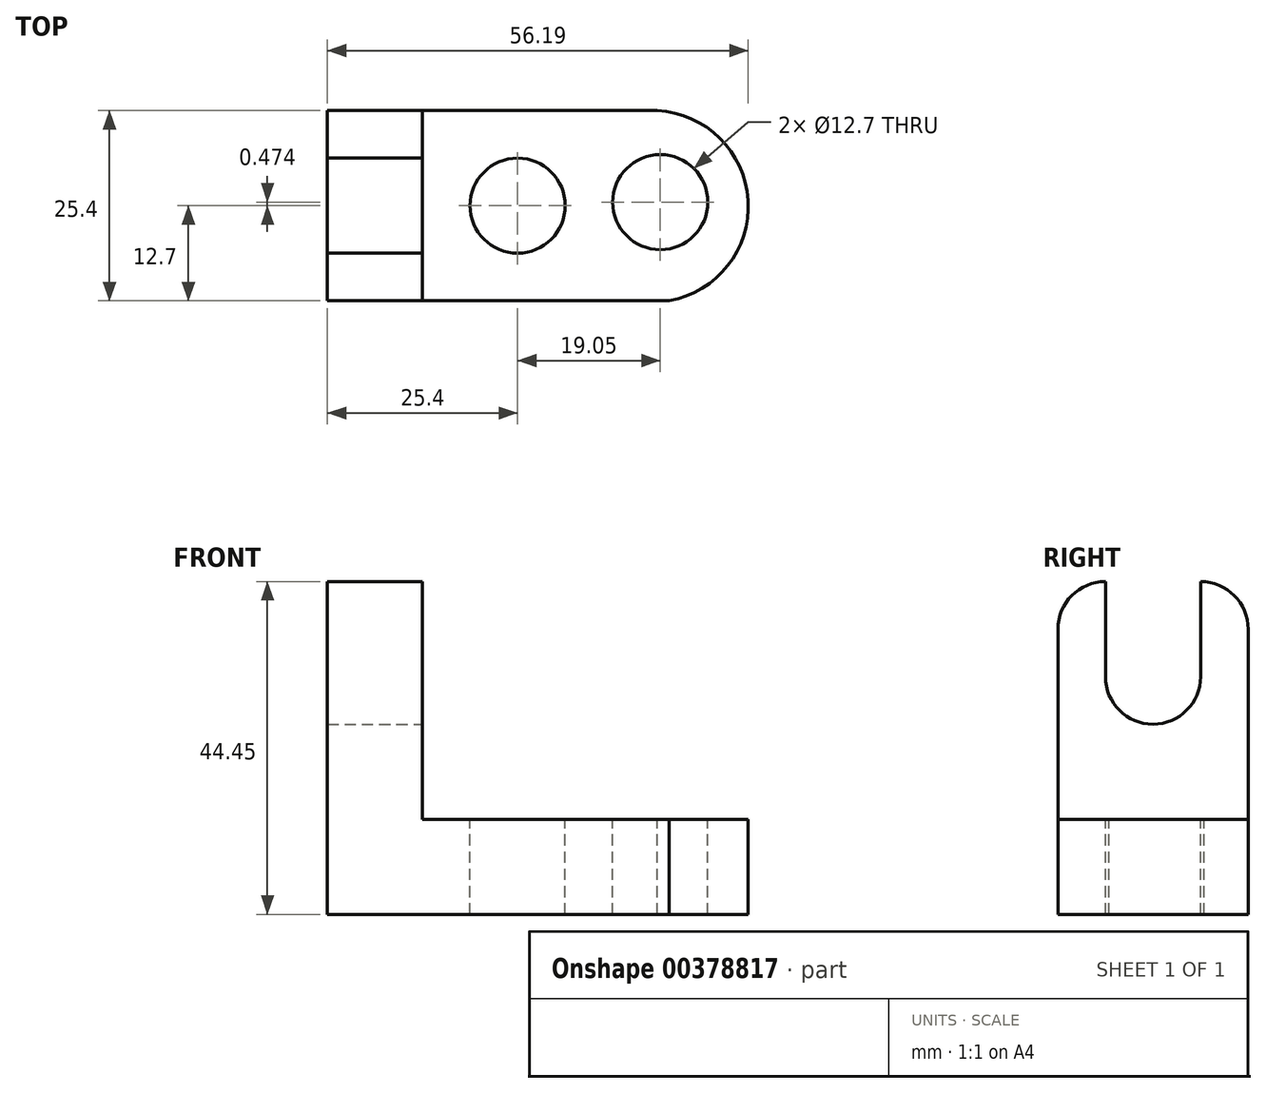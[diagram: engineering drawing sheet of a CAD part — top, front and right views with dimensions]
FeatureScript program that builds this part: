
annotation { "Feature Type Name" : "Feature", "Feature Type Description" : "" }
export const myFeature = defineFeature(function(context is Context, id is Id, definition is map)
    precondition{}
    {
        {
            var Q0;
            Q0=qCreatedBy(makeId("Front.planeOp"),FACE);
            var sketch = newSketch(context, id + "F0", { "sketchPlane" : qUnion([Q0])});
            skLineSegment(sketch, "E0", {"start": v(0, 0) * mm, "end": v(57.15, 0) * mm});
            skLineSegment(sketch, "E1", {"start": v(57.15, 0) * mm, "end": v(57.15, 12.7) * mm});
            skLineSegment(sketch, "E2", {"start": v(57.15, 12.7) * mm, "end": v(12.7, 12.7) * mm});
            skLineSegment(sketch, "E3", {"start": v(12.7, 12.7) * mm, "end": v(12.7, 44.45) * mm});
            skLineSegment(sketch, "E4", {"start": v(12.7, 44.45) * mm, "end": v(0, 44.45) * mm});
            skLineSegment(sketch, "E5", {"start": v(0, 44.45) * mm, "end": v(0, 0) * mm});
            skSolve(sketch);
        }
        {
            var Q0;
            Q0 = qSketchRegion(id + "F0", true);
            extrude(context, id + "F1", {"entities" : qUnion([Q0]), "depth" : 25.4 * mm});
        }
        {
            var Q0;
            Q0=makeQuery(id+"F1.opExtrude","SWEPT_FACE",FACE,{"disambiguationData":[OSD([sQuery(id+"F0.wireOp",EDGE,"E2")])]});
            var sketch = newSketch(context, id + "F2", { "sketchPlane" : qUnion([Q0])});
            skCircle(sketch, "E6", {"center": v(25.4, -12.7) * mm, "radius": 6.35 * mm});
            skPoint(sketch, "E6.centerSnap0", {"position": v(12.7, -12.7) * mm});
            skCircle(sketch, "E7", {"center": v(44.45, -12.23) * mm, "radius": 6.35 * mm});
            skSolve(sketch);
        }
        {
            var Q0;
            Q0=makeQuery(id+"F2.imprint","IMPRINT",FACE,{"disambiguationData":[TD([[makeQuery(id+"F2.imprint","IMPRINT",EDGE,{"derivedFrom":sQuery(id+"F2.wireOp",EDGE,"E6")}),-1.0]])]});
            var sketch = newSketch(context, id + "F3", { "sketchPlane" : qUnion([Q0])});
            skSolve(sketch);
        }
        {
            var Q0;
            Q0=makeQuery(id+"F2.imprint","IMPRINT",FACE,{"disambiguationData":[TD([[makeQuery(id+"F2.imprint","IMPRINT",EDGE,{"derivedFrom":sQuery(id+"F2.wireOp",EDGE,"E6")}),1.0]])]});
            var Q1;
            Q1=makeQuery(id+"F2.imprint","IMPRINT",FACE,{"disambiguationData":[TD([[makeQuery(id+"F2.imprint","IMPRINT",EDGE,{"derivedFrom":sQuery(id+"F2.wireOp",EDGE,"E7")}),1.0]])]});
            extrude(context, id + "F4", {"entities" : qUnion([Q0, Q1]), "operationType" : NewBodyOperationType.REMOVE, "oppositeDirection" : true, "depth" : 25.4 * mm});
        }
        {
            var Q0;
            Q0=makeQuery(id+"F3.imprint","IMPRINT",FACE,{"disambiguationData":[TD([[makeQuery(id+"F3.imprint","IMPRINT",EDGE,{"derivedFrom":makeQuery(id+"F2.imprint","IMPRINT",EDGE,{"derivedFrom":sQuery(id+"F2.wireOp",EDGE,"E6")})}),-1.0]])]});
            var sketch = newSketch(context, id + "F5", { "sketchPlane" : qUnion([Q0])});
            skArc(sketch, "E8", {"start": v(42.1, -25.54) * mm, "mid": v(56.19, -13.1) * mm, "end": v(42.71, 0) * mm});
            skSolve(sketch);
        }
        {
            var Q0;
            Q0 = qSketchRegion(id + "F5", true);
            var Q1;
            {var subQ1=sQuery(id+"F0.wireOp",EDGE,"E2");var subQ6=makeQuery(id+"F3.imprint","IMPRINT",EDGE,{"derivedFrom":makeQuery(id+"F2.imprint","IMPRINT",EDGE,{"derivedFrom":makeQuery(id+"F1.opExtrude","SWEPT_EDGE",EDGE,{"disambiguationData":[OSD([sQuery(id+"F0.wireOp",EDGE,"E1"),subQ1])]})})});Q1=makeQuery(id+"F5.imprint","IMPRINT",FACE,{"disambiguationData":[TD([[makeQuery(id+"F5.imprint","IMPRINT",EDGE,{"derivedFrom":subQ6}),1.0]])]});}
            extrude(context, id + "F6", {"entities" : qUnion([Q0, Q1]), "operationType" : NewBodyOperationType.REMOVE, "oppositeDirection" : true, "depth" : 25.4 * mm});
        }
        {
            var Q0;
            Q0=makeQuery(id+"F1.opExtrude","SWEPT_FACE",FACE,{"disambiguationData":[OSD([sQuery(id+"F0.wireOp",EDGE,"E3")])]});
            var sketch = newSketch(context, id + "F7", { "sketchPlane" : qUnion([Q0])});
            skCircle(sketch, "E9", {"center": v(-12.7, 31.75) * mm, "radius": 6.35 * mm});
            skLineSegment(sketch, "E10", {"start": v(-19.05, 31.75) * mm, "end": v(-19.05, 44.45) * mm});
            skLineSegment(sketch, "E11", {"start": v(-6.35, 31.75) * mm, "end": v(-6.35, 44.45) * mm});
            skSolve(sketch);
        }
        {
            var Q0;
            {var subQ0=sQuery(id+"F7.wireOp",EDGE,"E10");Q0=makeQuery(id+"F7.imprint","IMPRINT",FACE,{"disambiguationData":[TD([[makeQuery(id+"F7.imprint","IMPRINT",EDGE,{"derivedFrom":subQ0}),-1.0]])]});}
            var Q1;
            {var subQ0=sQuery(id+"F7.wireOp",EDGE,"E9");var subQ1=makeQuery(id+"F7.imprint","INTERSECT",VERTEX,{"derivedFrom":[subQ0,sQuery(id+"F7.wireOp",EDGE,"E10")]});Q1=makeQuery(id+"F7.imprint","IMPRINT",FACE,{"disambiguationData":[TD([[makeQuery(id+"F7.imprint","IMPRINT",EDGE,{"disambiguationData":[TD([[subQ1,1.0]])],"derivedFrom":subQ0}),1.0]])]});}
            extrude(context, id + "F8", {"entities" : qUnion([Q0, Q1]), "operationType" : NewBodyOperationType.REMOVE, "oppositeDirection" : true, "depth" : 25.4 * mm});
        }
        {
            var Q0;
            Q0=makeQuery(id+"F1.opExtrude","SWEPT_FACE",FACE,{"disambiguationData":[OSD([sQuery(id+"F0.wireOp",EDGE,"E3")])]});
            var sketch = newSketch(context, id + "F9", { "sketchPlane" : qUnion([Q0])});
            skArc(sketch, "E12", {"start": v(-19.05, 44.45) * mm, "mid": v(-23.54, 42.6) * mm, "end": v(-25.4, 38.1) * mm});
            skArc(sketch, "E13", {"start": v(0, 38.1) * mm, "mid": v(-1.86, 42.6) * mm, "end": v(-6.35, 44.45) * mm});
            skSolve(sketch);
        }
        {
            var Q0;
            {var subQ0=sQuery(id+"F9.wireOp",EDGE,"E12");Q0=makeQuery(id+"F9.imprint","IMPRINT",FACE,{"disambiguationData":[TD([[makeQuery(id+"F9.imprint","IMPRINT",EDGE,{"derivedFrom":subQ0}),-1.0]])]});}
            var Q1;
            {var subQ0=sQuery(id+"F9.wireOp",EDGE,"E13");Q1=makeQuery(id+"F9.imprint","IMPRINT",FACE,{"disambiguationData":[TD([[makeQuery(id+"F9.imprint","IMPRINT",EDGE,{"derivedFrom":subQ0}),-1.0]])]});}
            extrude(context, id + "F10", {"entities" : qUnion([Q0, Q1]), "operationType" : NewBodyOperationType.REMOVE, "oppositeDirection" : true, "depth" : 25.4 * mm});
        }
    });
